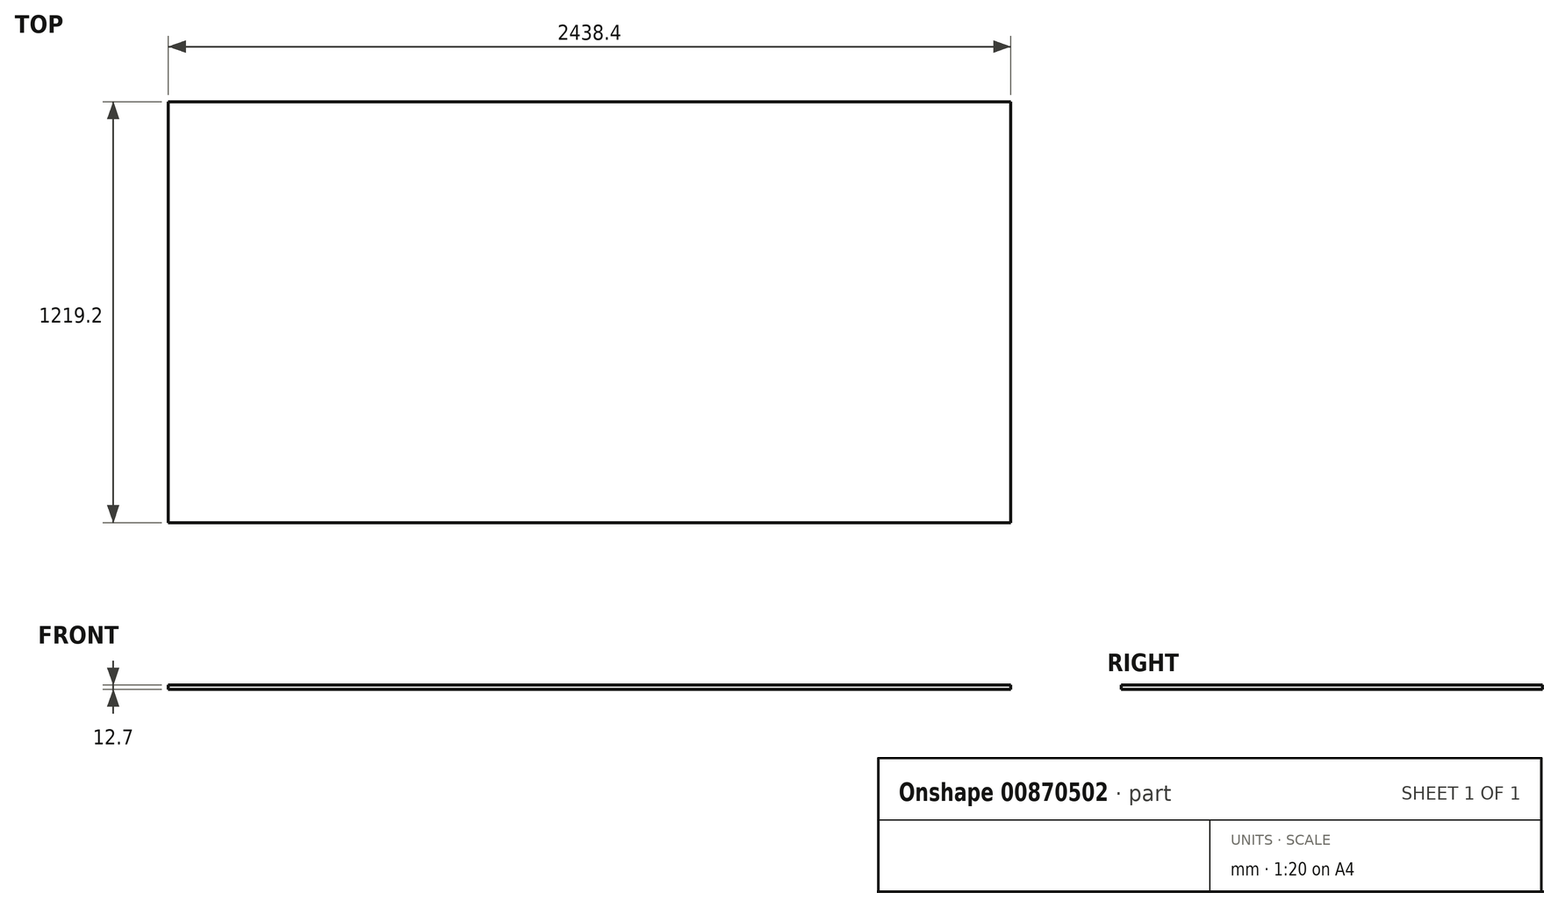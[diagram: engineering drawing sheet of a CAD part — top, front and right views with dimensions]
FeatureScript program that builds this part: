
annotation { "Feature Type Name" : "Feature", "Feature Type Description" : "" }
export const myFeature = defineFeature(function(context is Context, id is Id, definition is map)
    precondition{}
    {
        {
            var Q0;
            Q0=qCreatedBy(makeId("Top.planeOp"),FACE);
            var sketch = newSketch(context, id + "F0", { "sketchPlane" : qUnion([Q0])});
            skLineSegment(sketch, "E0.bottom", {"start": v(0, 0) * mm, "end": v(2438.4, 0) * mm});
            skLineSegment(sketch, "E0.top", {"start": v(0, -1219.2) * mm, "end": v(2438.4, -1219.2) * mm});
            skLineSegment(sketch, "E0.left", {"start": v(0, 0) * mm, "end": v(0, -1219.2) * mm});
            skLineSegment(sketch, "E0.right", {"start": v(2438.4, 0) * mm, "end": v(2438.4, -1219.2) * mm});
            skSolve(sketch);
        }
        {
            var Q0;
            Q0 = qSketchRegion(id + "F0", true);
            extrude(context, id + "F1", {"entities" : qUnion([Q0]), "depth" : 12.7 * mm, "offsetDistance" : 25.4 * mm});
        }
    });
